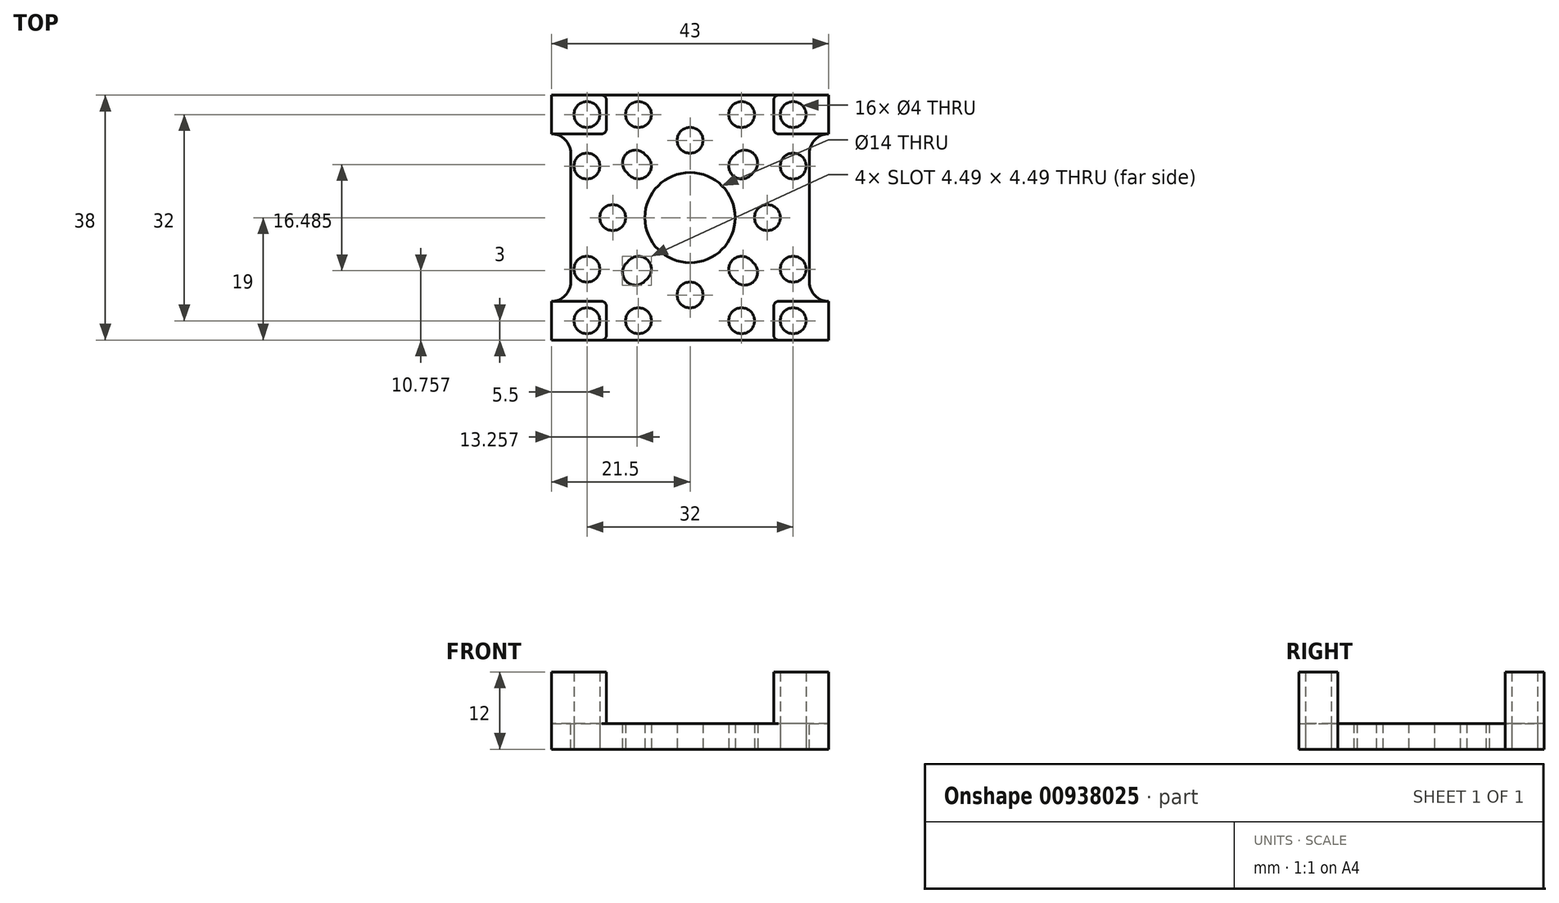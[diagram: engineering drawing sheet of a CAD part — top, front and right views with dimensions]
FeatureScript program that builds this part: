
annotation { "Feature Type Name" : "Feature", "Feature Type Description" : "" }
export const myFeature = defineFeature(function(context is Context, id is Id, definition is map)
    precondition{}
    {
        {
            var Q0;
            Q0=qCreatedBy(makeId("Top.planeOp"),FACE);
            var sketch = newSketch(context, id + "F0", { "sketchPlane" : qUnion([Q0]) });
            skCircle(sketch, "E0", {"center": v(0, 0) * mm, "radius": 7 * mm});
            skCircle(sketch, "E1", {"center": v(0, 12) * mm, "radius": 2 * mm});
            skCircle(sketch, "E2", {"center": v(0, -12) * mm, "radius": 2 * mm});
            skCircle(sketch, "E3", {"center": v(12, 0) * mm, "radius": 2 * mm});
            skCircle(sketch, "E4", {"center": v(-12, 0) * mm, "radius": 2 * mm});
            skLineSegment(sketch, "E5", {"start": v(0, 12) * mm, "end": v(0, 0) * mm, "construction": true});
            skLineSegment(sketch, "E6", {"start": v(0, -12) * mm, "end": v(0, 0) * mm, "construction": true});
            skLineSegment(sketch, "E7", {"start": v(12, 0) * mm, "end": v(0, 0) * mm, "construction": true});
            skLineSegment(sketch, "E8", {"start": v(-12, 0) * mm, "end": v(0, 0) * mm, "construction": true});
            skLineSegment(sketch, "E9.bottom", {"start": v(8, 8) * mm, "end": v(-8, 8) * mm, "construction": true});
            skLineSegment(sketch, "E9.top", {"start": v(8, -8) * mm, "end": v(-8, -8) * mm, "construction": true});
            skLineSegment(sketch, "E9.left", {"start": v(8, 8) * mm, "end": v(8, -8) * mm, "construction": true});
            skLineSegment(sketch, "E9.right", {"start": v(-8, 8) * mm, "end": v(-8, -8) * mm, "construction": true});
            skArc(sketch, "E10", {"start": v(6.59, 9.41) * mm, "mid": v(6.59, 6.59) * mm, "end": v(9.41, 6.59) * mm});
            skArc(sketch, "E11", {"start": v(-9.41, 6.59) * mm, "mid": v(-6.59, 6.59) * mm, "end": v(-6.59, 9.41) * mm});
            skArc(sketch, "E12", {"start": v(-6.59, -9.41) * mm, "mid": v(-6.59, -6.59) * mm, "end": v(-9.41, -6.59) * mm});
            skArc(sketch, "E13", {"start": v(9.41, -6.59) * mm, "mid": v(6.59, -6.59) * mm, "end": v(6.59, -9.41) * mm});
            skLineSegment(sketch, "E14", {"start": v(0, 0) * mm, "end": v(-8.49, 8.49) * mm, "construction": true});
            skArc(sketch, "E15", {"start": v(-7.07, 9.9) * mm, "mid": v(-9.9, 9.9) * mm, "end": v(-9.9, 7.07) * mm});
            skLineSegment(sketch, "E16", {"start": v(0, 0) * mm, "end": v(8.49, 8.49) * mm, "construction": true});
            skLineSegment(sketch, "E17", {"start": v(0, 0) * mm, "end": v(8.49, -8.49) * mm, "construction": true});
            skLineSegment(sketch, "E18", {"start": v(0, 0) * mm, "end": v(-8.49, -8.49) * mm, "construction": true});
            skArc(sketch, "E19", {"start": v(7.07, -9.9) * mm, "mid": v(9.9, -9.9) * mm, "end": v(9.9, -7.07) * mm});
            skArc(sketch, "E20", {"start": v(-9.9, -7.07) * mm, "mid": v(-9.9, -9.9) * mm, "end": v(-7.07, -9.9) * mm});
            skLineSegment(sketch, "E21", {"start": v(-6.59, 9.41) * mm, "end": v(-7.07, 9.9) * mm});
            skLineSegment(sketch, "E22", {"start": v(-9.9, 7.07) * mm, "end": v(-9.41, 6.59) * mm});
            skLineSegment(sketch, "E23", {"start": v(9.9, 7.07) * mm, "end": v(9.41, 6.59) * mm});
            skLineSegment(sketch, "E24", {"start": v(7.07, 9.9) * mm, "end": v(6.59, 9.41) * mm});
            skLineSegment(sketch, "E25", {"start": v(9.41, -6.59) * mm, "end": v(9.9, -7.07) * mm});
            skLineSegment(sketch, "E26", {"start": v(6.59, -9.41) * mm, "end": v(7.07, -9.9) * mm});
            skLineSegment(sketch, "E27", {"start": v(-9.41, -6.59) * mm, "end": v(-9.9, -7.07) * mm});
            skLineSegment(sketch, "E28", {"start": v(-6.59, -9.41) * mm, "end": v(-7.07, -9.9) * mm});
            skArc(sketch, "E29.trimOffspring", {"start": v(9.9, 7.07) * mm, "mid": v(9.9, 9.9) * mm, "end": v(7.07, 9.9) * mm});
            skLineSegment(sketch, "E30.bottom", {"start": v(0, 0) * mm, "end": v(16, 0) * mm, "construction": true});
            skLineSegment(sketch, "E30.top", {"start": v(0, 16) * mm, "end": v(16, 16) * mm, "construction": true});
            skLineSegment(sketch, "E30.left", {"start": v(0, 0) * mm, "end": v(0, 16) * mm, "construction": true});
            skLineSegment(sketch, "E30.right", {"start": v(16, 0) * mm, "end": v(16, 16) * mm, "construction": true});
            skCircle(sketch, "E31", {"center": v(16, 16) * mm, "radius": 2 * mm});
            skCircle(sketch, "E32", {"center": v(8, 16) * mm, "radius": 2 * mm});
            skCircle(sketch, "E33", {"center": v(16, 8) * mm, "radius": 2 * mm});
            skPoint(sketch, "E33.perimeterSnap0", {"position": v(16, 8) * mm});
            skCircle(sketch, "E34.1.0", {"center": v(-16, 8) * mm, "radius": 2 * mm});
            skCircle(sketch, "E34.1.1", {"center": v(-16, 16) * mm, "radius": 2 * mm});
            skCircle(sketch, "E34.1.2", {"center": v(-8, 16) * mm, "radius": 2 * mm});
            skCircle(sketch, "E34.2.0", {"center": v(-8, -16) * mm, "radius": 2 * mm});
            skCircle(sketch, "E34.2.1", {"center": v(-16, -16) * mm, "radius": 2 * mm});
            skCircle(sketch, "E34.2.2", {"center": v(-16, -8) * mm, "radius": 2 * mm});
            skCircle(sketch, "E34.3.0", {"center": v(16, -8) * mm, "radius": 2 * mm});
            skCircle(sketch, "E34.3.1", {"center": v(16, -16) * mm, "radius": 2 * mm});
            skCircle(sketch, "E34.3.2", {"center": v(8, -16) * mm, "radius": 2 * mm});
            skLineSegment(sketch, "E35.bottom", {"start": v(21.5, 19) * mm, "end": v(-21.5, 19) * mm});
            skLineSegment(sketch, "E35.top", {"start": v(21.5, -19) * mm, "end": v(-21.5, -19) * mm});
            skLineSegment(sketch, "E35.left", {"start": v(21.5, 19) * mm, "end": v(21.5, -19) * mm});
            skLineSegment(sketch, "E35.right", {"start": v(-21.5, 19) * mm, "end": v(-21.5, -19) * mm});
            skSolve(sketch);
        }
        {
            var Q0;
            Q0=qSketchRegion(id+"F0",true);
            extrude(context, id + "F1", {"entities" : qUnion([Q0]), "depth" : 4 * mm, "offsetDistance" : 25 * mm});
        }
        {
            var Q0;
            Q0=makeQuery(id+"F1.opExtrude","CAP_FACE",FACE,{"disambiguationData":[OSD([sQuery(id+"F0.wireOp",EDGE,"E0"),sQuery(id+"F0.wireOp",EDGE,"E1"),sQuery(id+"F0.wireOp",EDGE,"E2"),sQuery(id+"F0.wireOp",EDGE,"E3"),sQuery(id+"F0.wireOp",EDGE,"E4"),sQuery(id+"F0.wireOp",EDGE,"E10"),sQuery(id+"F0.wireOp",EDGE,"E11"),sQuery(id+"F0.wireOp",EDGE,"E12"),sQuery(id+"F0.wireOp",EDGE,"E13"),sQuery(id+"F0.wireOp",EDGE,"E15"),sQuery(id+"F0.wireOp",EDGE,"E19"),sQuery(id+"F0.wireOp",EDGE,"E20"),sQuery(id+"F0.wireOp",EDGE,"E21"),sQuery(id+"F0.wireOp",EDGE,"E22"),sQuery(id+"F0.wireOp",EDGE,"E23"),sQuery(id+"F0.wireOp",EDGE,"E24"),sQuery(id+"F0.wireOp",EDGE,"E25"),sQuery(id+"F0.wireOp",EDGE,"E26"),sQuery(id+"F0.wireOp",EDGE,"E27"),sQuery(id+"F0.wireOp",EDGE,"E28"),sQuery(id+"F0.wireOp",EDGE,"E29.trimOffspring"),sQuery(id+"F0.wireOp",EDGE,"E31"),sQuery(id+"F0.wireOp",EDGE,"E32"),sQuery(id+"F0.wireOp",EDGE,"E33"),sQuery(id+"F0.wireOp",EDGE,"E34.1.0"),sQuery(id+"F0.wireOp",EDGE,"E34.1.1"),sQuery(id+"F0.wireOp",EDGE,"E34.1.2"),sQuery(id+"F0.wireOp",EDGE,"E34.2.0"),sQuery(id+"F0.wireOp",EDGE,"E34.2.1"),sQuery(id+"F0.wireOp",EDGE,"E34.2.2"),sQuery(id+"F0.wireOp",EDGE,"E34.3.0"),sQuery(id+"F0.wireOp",EDGE,"E34.3.1"),sQuery(id+"F0.wireOp",EDGE,"E34.3.2"),sQuery(id+"F0.wireOp",EDGE,"E35.bottom"),sQuery(id+"F0.wireOp",EDGE,"E35.top"),sQuery(id+"F0.wireOp",EDGE,"E35.left"),sQuery(id+"F0.wireOp",EDGE,"E35.right")])],"isStart":false});
            var sketch = newSketch(context, id + "F2", { "sketchPlane" : qUnion([Q0]) });
            skLineSegment(sketch, "E36.0", {"start": v(21.5, 19) * mm, "end": v(-21.5, 19) * mm, "construction": true});
            skLineSegment(sketch, "E37.0", {"start": v(-21.5, 19) * mm, "end": v(-21.5, -19) * mm, "construction": true});
            skLineSegment(sketch, "E38.bottom", {"start": v(-21.5, 19) * mm, "end": v(-13, 19) * mm});
            skLineSegment(sketch, "E38.top", {"start": v(-21.5, 13) * mm, "end": v(-13, 13) * mm});
            skLineSegment(sketch, "E38.left", {"start": v(-21.5, 19) * mm, "end": v(-21.5, 13) * mm});
            skLineSegment(sketch, "E38.right", {"start": v(-13, 19) * mm, "end": v(-13, 13) * mm});
            skLineSegment(sketch, "E39.bottom", {"start": v(21.5, 19) * mm, "end": v(13, 19) * mm});
            skLineSegment(sketch, "E39.top", {"start": v(21.5, 13) * mm, "end": v(13, 13) * mm});
            skLineSegment(sketch, "E39.left", {"start": v(21.5, 19) * mm, "end": v(21.5, 13) * mm});
            skLineSegment(sketch, "E39.right", {"start": v(13, 19) * mm, "end": v(13, 13) * mm});
            skLineSegment(sketch, "E40.1.0", {"start": v(13, -19) * mm, "end": v(13, -13) * mm});
            skLineSegment(sketch, "E40.1.1", {"start": v(-13, -19) * mm, "end": v(-13, -13) * mm});
            skLineSegment(sketch, "E40.1.2", {"start": v(-21.5, -19) * mm, "end": v(21.5, -19) * mm, "construction": true});
            skLineSegment(sketch, "E40.1.3", {"start": v(21.5, -19) * mm, "end": v(21.5, -13) * mm});
            skLineSegment(sketch, "E40.1.4", {"start": v(-21.5, -13) * mm, "end": v(-13, -13) * mm});
            skLineSegment(sketch, "E40.1.5", {"start": v(21.5, -13) * mm, "end": v(13, -13) * mm});
            skLineSegment(sketch, "E40.1.6", {"start": v(-21.5, -19) * mm, "end": v(-21.5, -13) * mm});
            skLineSegment(sketch, "E40.1.7", {"start": v(21.5, -19) * mm, "end": v(13, -19) * mm});
            skLineSegment(sketch, "E40.1.8", {"start": v(-21.5, -19) * mm, "end": v(-13, -19) * mm});
            skPoint(sketch, "E40.center", {"position": v(0, 0) * mm});
            skCircle(sketch, "E41.0", {"center": v(-16, 16) * mm, "radius": 2 * mm});
            skCircle(sketch, "E42.0", {"center": v(16, 16) * mm, "radius": 2 * mm});
            skCircle(sketch, "E43.0", {"center": v(16, -16) * mm, "radius": 2 * mm});
            skCircle(sketch, "E44.0", {"center": v(-16, -16) * mm, "radius": 2 * mm});
            skSolve(sketch);
        }
        {
            var Q0;
            Q0=qSketchRegion(id+"F2",true);
            extrude(context, id + "F3", {"entities" : qUnion([Q0]), "operationType" : NewBodyOperationType.ADD, "depth" : 8 * mm, "offsetDistance" : 25 * mm});
        }
        {
            var Q0;
            Q0=makeQuery(id+"F1.opExtrude","CAP_FACE",FACE,{"disambiguationData":[OSD([sQuery(id+"F0.wireOp",EDGE,"E0"),sQuery(id+"F0.wireOp",EDGE,"E1"),sQuery(id+"F0.wireOp",EDGE,"E2"),sQuery(id+"F0.wireOp",EDGE,"E3"),sQuery(id+"F0.wireOp",EDGE,"E4"),sQuery(id+"F0.wireOp",EDGE,"E10"),sQuery(id+"F0.wireOp",EDGE,"E11"),sQuery(id+"F0.wireOp",EDGE,"E12"),sQuery(id+"F0.wireOp",EDGE,"E13"),sQuery(id+"F0.wireOp",EDGE,"E15"),sQuery(id+"F0.wireOp",EDGE,"E19"),sQuery(id+"F0.wireOp",EDGE,"E20"),sQuery(id+"F0.wireOp",EDGE,"E21"),sQuery(id+"F0.wireOp",EDGE,"E22"),sQuery(id+"F0.wireOp",EDGE,"E23"),sQuery(id+"F0.wireOp",EDGE,"E24"),sQuery(id+"F0.wireOp",EDGE,"E25"),sQuery(id+"F0.wireOp",EDGE,"E26"),sQuery(id+"F0.wireOp",EDGE,"E27"),sQuery(id+"F0.wireOp",EDGE,"E28"),sQuery(id+"F0.wireOp",EDGE,"E29.trimOffspring"),sQuery(id+"F0.wireOp",EDGE,"E31"),sQuery(id+"F0.wireOp",EDGE,"E32"),sQuery(id+"F0.wireOp",EDGE,"E33"),sQuery(id+"F0.wireOp",EDGE,"E34.1.0"),sQuery(id+"F0.wireOp",EDGE,"E34.1.1"),sQuery(id+"F0.wireOp",EDGE,"E34.1.2"),sQuery(id+"F0.wireOp",EDGE,"E34.2.0"),sQuery(id+"F0.wireOp",EDGE,"E34.2.1"),sQuery(id+"F0.wireOp",EDGE,"E34.2.2"),sQuery(id+"F0.wireOp",EDGE,"E34.3.0"),sQuery(id+"F0.wireOp",EDGE,"E34.3.1"),sQuery(id+"F0.wireOp",EDGE,"E34.3.2"),sQuery(id+"F0.wireOp",EDGE,"E35.bottom"),sQuery(id+"F0.wireOp",EDGE,"E35.top"),sQuery(id+"F0.wireOp",EDGE,"E35.left"),sQuery(id+"F0.wireOp",EDGE,"E35.right")])],"isStart":false});
            var sketch = newSketch(context, id + "F4", { "sketchPlane" : qUnion([Q0]) });
            skPoint(sketch, "E45.0", {"position": v(-21.5, 13) * mm});
            skPoint(sketch, "E46.0", {"position": v(-21.5, -13) * mm});
            skLineSegment(sketch, "E47.bottom", {"start": v(-21.5, 13) * mm, "end": v(-18.5, 13) * mm});
            skLineSegment(sketch, "E47.top", {"start": v(-21.5, -13) * mm, "end": v(-18.5, -13) * mm});
            skLineSegment(sketch, "E47.left", {"start": v(-21.5, 13) * mm, "end": v(-21.5, -13) * mm});
            skLineSegment(sketch, "E47.right", {"start": v(-18.5, 13) * mm, "end": v(-18.5, -13) * mm});
            skLineSegment(sketch, "E48.1.0", {"start": v(21.5, 13) * mm, "end": v(18.5, 13) * mm});
            skLineSegment(sketch, "E48.1.1", {"start": v(21.5, -13) * mm, "end": v(18.5, -13) * mm});
            skLineSegment(sketch, "E48.1.2", {"start": v(18.5, -13) * mm, "end": v(18.5, 13) * mm});
            skPoint(sketch, "E48.1.3", {"position": v(21.5, 13) * mm});
            skLineSegment(sketch, "E48.1.4", {"start": v(21.5, -13) * mm, "end": v(21.5, 13) * mm});
            skPoint(sketch, "E48.1.5", {"position": v(21.5, -13) * mm});
            skPoint(sketch, "E48.center", {"position": v(0, 0) * mm});
            skSolve(sketch);
        }
        {
            var Q0;
            Q0=qSketchRegion(id+"F4",true);
            extrude(context, id + "F5", {"entities" : qUnion([Q0]), "operationType" : NewBodyOperationType.REMOVE, "oppositeDirection" : true, "depth" : 25 * mm, "offsetDistance" : 25 * mm});
        }
        {
            var Q0;
            Q0=makeQuery(id+"F5.boolean.opBoolean","COPY",EDGE,{"derivedFrom":makeQuery(id+"F5.opExtrude","SWEPT_EDGE",EDGE,{"disambiguationData":[OSD([sQuery(id+"F2.wireOp",EDGE,"E38.top"),sQuery(id+"F4.wireOp",EDGE,"E47.bottom"),sQuery(id+"F4.wireOp",EDGE,"E47.right")])]})});
            var Q1;
            Q1=makeQuery(id+"F5.boolean.opBoolean","COPY",EDGE,{"derivedFrom":makeQuery(id+"F5.opExtrude","SWEPT_EDGE",EDGE,{"disambiguationData":[OSD([sQuery(id+"F2.wireOp",EDGE,"E40.1.4"),sQuery(id+"F4.wireOp",EDGE,"E47.top"),sQuery(id+"F4.wireOp",EDGE,"E47.right")])]})});
            var Q2;
            Q2=makeQuery(id+"F5.boolean.opBoolean","COPY",EDGE,{"derivedFrom":makeQuery(id+"F5.opExtrude","SWEPT_EDGE",EDGE,{"disambiguationData":[OSD([sQuery(id+"F2.wireOp",EDGE,"E39.top"),sQuery(id+"F4.wireOp",EDGE,"E48.1.0"),sQuery(id+"F4.wireOp",EDGE,"E48.1.2")])]})});
            var Q3;
            Q3=makeQuery(id+"F5.boolean.opBoolean","COPY",EDGE,{"derivedFrom":makeQuery(id+"F5.opExtrude","SWEPT_EDGE",EDGE,{"disambiguationData":[OSD([sQuery(id+"F2.wireOp",EDGE,"E40.1.5"),sQuery(id+"F4.wireOp",EDGE,"E48.1.1"),sQuery(id+"F4.wireOp",EDGE,"E48.1.2")])]})});
            fillet(context, id + "F6", {"entities" : qUnion([Q0, Q1, Q2, Q3]), "radius" : 3 * mm, "tangentPropagation" : true, "conicFillet" : false});
        }
        {
            var Q0;
            Q0=makeQuery(id+"F3.opExtrude","SWEPT_EDGE",EDGE,{"disambiguationData":[OSD([sQuery(id+"F2.wireOp",EDGE,"E39.top"),sQuery(id+"F2.wireOp",EDGE,"E39.right")])]});
            var Q1;
            Q1=makeQuery(id+"F3.opExtrude","SWEPT_EDGE",EDGE,{"disambiguationData":[OSD([sQuery(id+"F0.wireOp",EDGE,"E35.top"),sQuery(id+"F2.wireOp",EDGE,"E40.1.0"),sQuery(id+"F2.wireOp",EDGE,"E40.1.7")])]});
            var Q2;
            Q2=makeQuery(id+"F3.opExtrude","SWEPT_EDGE",EDGE,{"disambiguationData":[OSD([sQuery(id+"F2.wireOp",EDGE,"E40.1.0"),sQuery(id+"F2.wireOp",EDGE,"E40.1.5")])]});
            var Q3;
            Q3=makeQuery(id+"F3.opExtrude","SWEPT_EDGE",EDGE,{"disambiguationData":[OSD([sQuery(id+"F0.wireOp",EDGE,"E35.top"),sQuery(id+"F2.wireOp",EDGE,"E40.1.1"),sQuery(id+"F2.wireOp",EDGE,"E40.1.8")])]});
            var Q4;
            Q4=makeQuery(id+"F3.opExtrude","SWEPT_EDGE",EDGE,{"disambiguationData":[OSD([sQuery(id+"F2.wireOp",EDGE,"E38.top"),sQuery(id+"F2.wireOp",EDGE,"E38.right")])]});
            var Q5;
            Q5=makeQuery(id+"F3.opExtrude","SWEPT_EDGE",EDGE,{"disambiguationData":[OSD([sQuery(id+"F0.wireOp",EDGE,"E35.bottom"),sQuery(id+"F2.wireOp",EDGE,"E38.bottom"),sQuery(id+"F2.wireOp",EDGE,"E38.right")])]});
            var Q6;
            Q6=makeQuery(id+"F3.opExtrude","SWEPT_EDGE",EDGE,{"disambiguationData":[OSD([sQuery(id+"F2.wireOp",EDGE,"E40.1.1"),sQuery(id+"F2.wireOp",EDGE,"E40.1.4")])]});
            var Q7;
            Q7=makeQuery(id+"F3.opExtrude","SWEPT_EDGE",EDGE,{"disambiguationData":[OSD([sQuery(id+"F0.wireOp",EDGE,"E35.bottom"),sQuery(id+"F2.wireOp",EDGE,"E39.bottom"),sQuery(id+"F2.wireOp",EDGE,"E39.right")])]});
            fillet(context, id + "F7", {"entities" : qUnion([Q0, Q1, Q2, Q3, Q4, Q5, Q6, Q7]), "radius" : 0.7 * mm, "tangentPropagation" : true, "conicFillet" : false});
        }
    });
